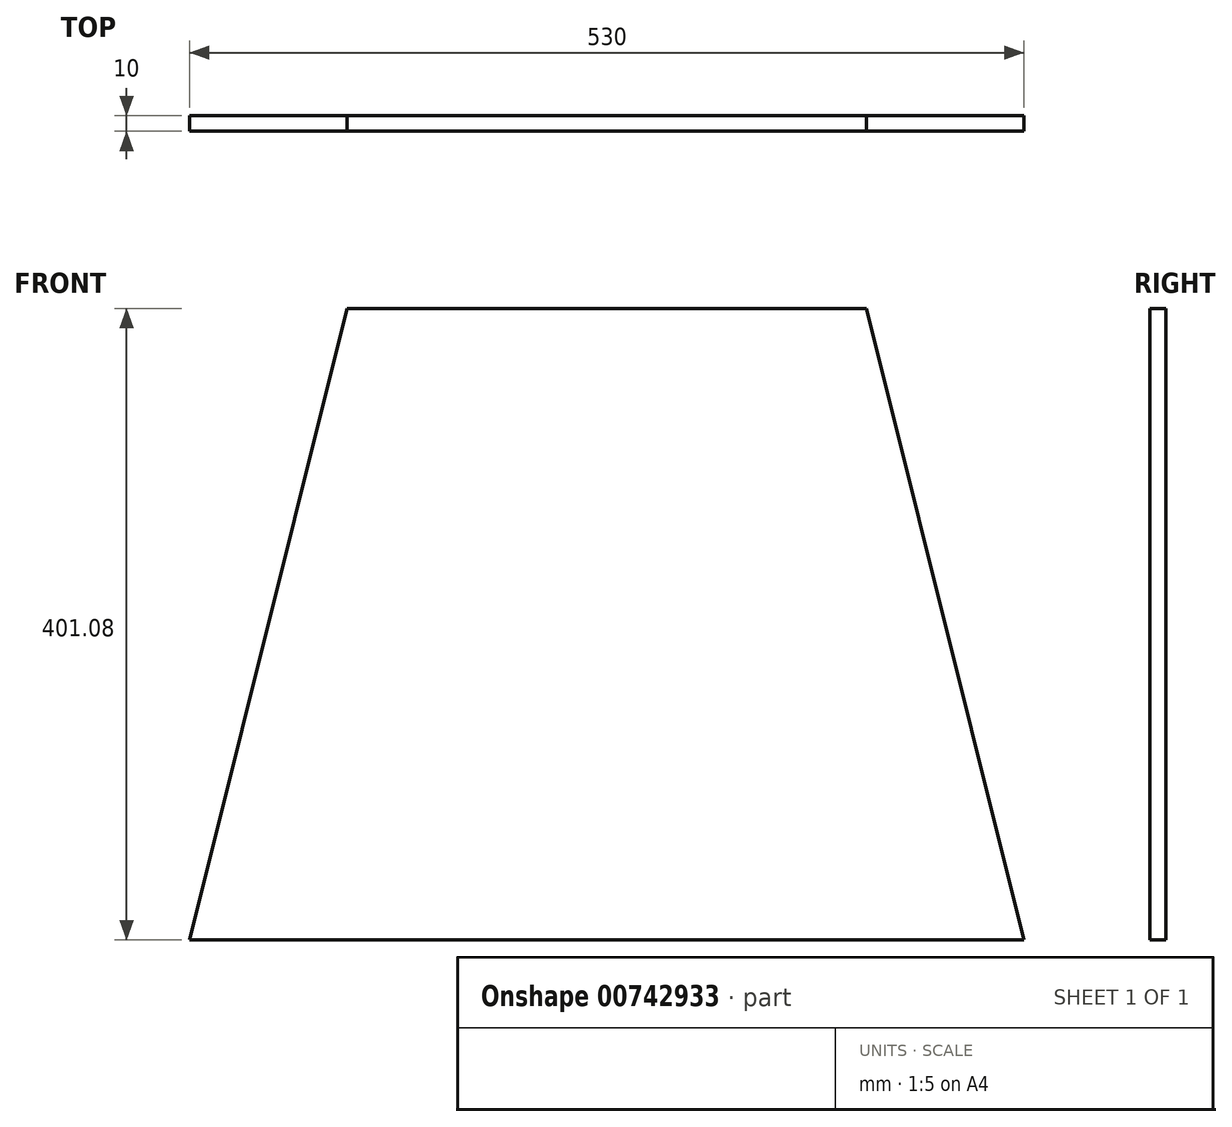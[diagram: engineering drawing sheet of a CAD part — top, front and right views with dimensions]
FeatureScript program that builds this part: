
annotation { "Feature Type Name" : "Feature", "Feature Type Description" : "" }
export const myFeature = defineFeature(function(context is Context, id is Id, definition is map)
    precondition{}
    {
        {
            var Q0;
            Q0=qCreatedBy(makeId("Front.planeOp"),FACE);
            var sketch = newSketch(context, id + "F0", { "sketchPlane" : qUnion([Q0])});
            skLineSegment(sketch, "E0", {"start": v(0, 0) * mm, "end": v(-90.1, 0) * mm, "construction": true});
            skSolve(sketch);
        }
        {
            var Q0;
            Q0=qCreatedBy(makeId("Front.planeOp"),FACE);
            var sketch = newSketch(context, id + "F1", { "sketchPlane" : qUnion([Q0])});
            skLineSegment(sketch, "E1", {"start": v(0, 0) * mm, "end": v(-265, 0) * mm});
            skLineSegment(sketch, "E2", {"start": v(-265, 0) * mm, "end": v(-165, 401.08) * mm});
            skLineSegment(sketch, "E3", {"start": v(-165, 401.08) * mm, "end": v(0, 401.08) * mm});
            skLineSegment(sketch, "E4.MirrorCS", {"start": v(0, 0) * mm, "end": v(265, 0) * mm});
            skLineSegment(sketch, "E5.MirrorCS", {"start": v(265, 0) * mm, "end": v(165, 401.08) * mm});
            skLineSegment(sketch, "E6.MirrorCS", {"start": v(165, 401.08) * mm, "end": v(0, 401.08) * mm});
            skSolve(sketch);
        }
        {
            var Q0;
            Q0=makeQuery(id+"F1.imprint","IMPRINT",FACE,{"disambiguationData":[TD([[makeQuery(id+"F1.imprint","IMPRINT",EDGE,{"derivedFrom":sQuery(id+"F1.wireOp",EDGE,"E1")}),-1.0]])]});
            extrude(context, id + "F2", {"entities" : qUnion([Q0]), "depth" : 10 * mm, "offsetDistance" : 25 * mm});
        }
    });
